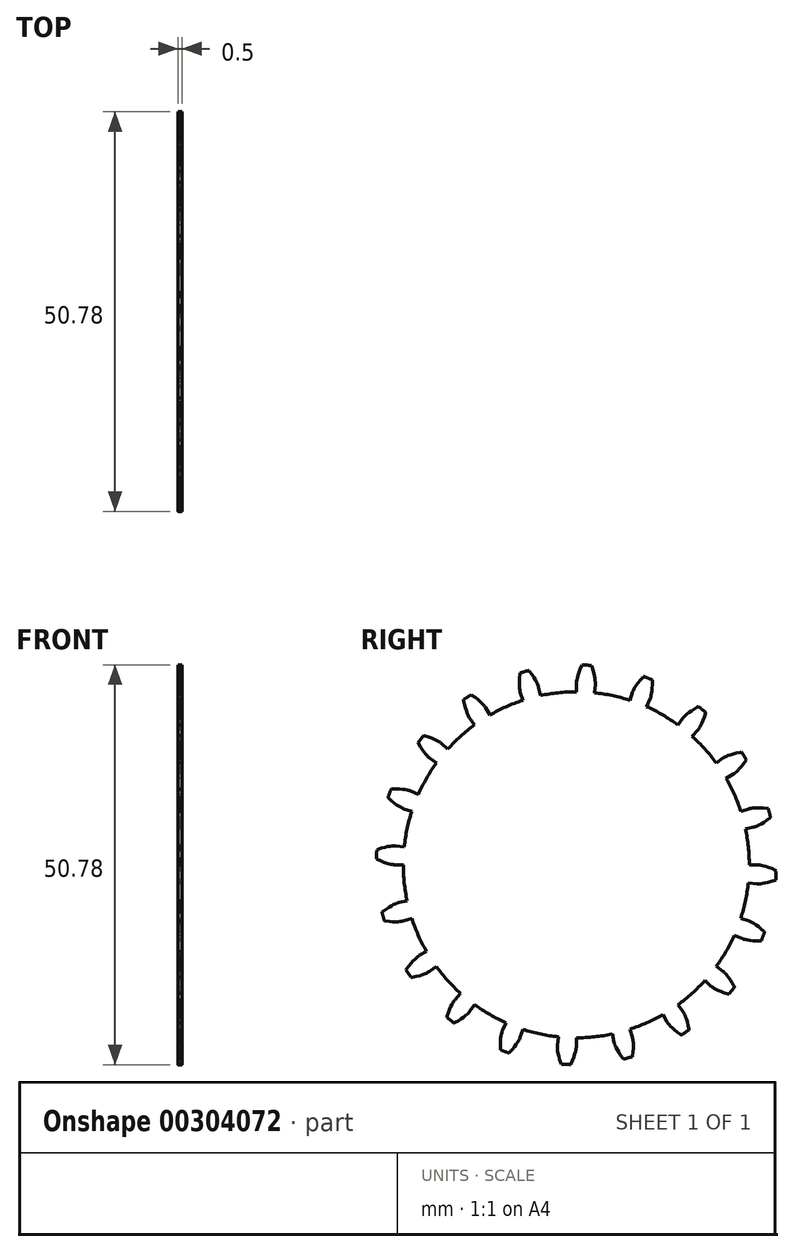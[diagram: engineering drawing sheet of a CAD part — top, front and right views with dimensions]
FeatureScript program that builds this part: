
annotation { "Feature Type Name" : "Feature", "Feature Type Description" : "" }
export const myFeature = defineFeature(function(context is Context, id is Id, definition is map)
    precondition{}
    {
        {
            assignVariable(context, id + "F0", {"name" : "GearThickness", "anyValue" : .5});
        }
        {
            var Q0;
            Q0=qCreatedBy(makeId("Right.planeOp"),FACE);
            var sketch = newSketch(context, id + "F1", { "sketchPlane" : qUnion([Q0])});
            skCircle(sketch, "E0", {"center": v(0, 0) * mm, "radius": 21.98 * mm});
            skCircle(sketch, "E1", {"center": v(0, 0) * mm, "radius": 23.05 * mm, "construction": true});
            skCircle(sketch, "E2", {"center": v(0, 0) * mm, "radius": 23.81 * mm, "construction": true});
            skCircle(sketch, "E3", {"center": v(0, 0) * mm, "radius": 25.4 * mm});
            skLineSegment(sketch, "E4", {"start": v(0, 0) * mm, "end": v(-23.05, 0) * mm, "construction": true});
            skLineSegment(sketch, "E5.1.0", {"start": v(0, 0) * mm, "end": v(-23.03, 1.15) * mm, "construction": true});
            skLineSegment(sketch, "E5.2.0", {"start": v(0, 0) * mm, "end": v(-22.94, 2.3) * mm, "construction": true});
            skLineSegment(sketch, "E5.3.0", {"start": v(0, 0) * mm, "end": v(-22.8, 3.45) * mm, "construction": true});
            skLineSegment(sketch, "E5.4.0", {"start": v(0, 0) * mm, "end": v(-22.6, 4.58) * mm, "construction": true});
            skLineSegment(sketch, "E5.5.0", {"start": v(0, 0) * mm, "end": v(-22.34, 5.7) * mm, "construction": true});
            skLineSegment(sketch, "E5.6.0", {"start": v(0, 0) * mm, "end": v(-22.02, 6.81) * mm, "construction": true});
            skLineSegment(sketch, "E5.7.0", {"start": v(0, 0) * mm, "end": v(-21.66, 7.9) * mm, "construction": true});
            skLineSegment(sketch, "E5.8.0", {"start": v(0, 0) * mm, "end": v(-21.23, 8.98) * mm, "construction": true});
            skLineSegment(sketch, "E5.9.0", {"start": v(0, 0) * mm, "end": v(-20.76, 10.03) * mm, "construction": true});
            skLineSegment(sketch, "E5.10.0", {"start": v(0, 0) * mm, "end": v(-20.23, 11.05) * mm, "construction": true});
            skLineSegment(sketch, "E5.11.0", {"start": v(0, 0) * mm, "end": v(-19.65, 12.05) * mm, "construction": true});
            skLineSegment(sketch, "E5.12.0", {"start": v(0, 0) * mm, "end": v(-19.03, 13.02) * mm, "construction": true});
            skLineSegment(sketch, "E5.13.0", {"start": v(0, 0) * mm, "end": v(-18.35, 13.95) * mm, "construction": true});
            skLineSegment(sketch, "E5.14.0", {"start": v(0, 0) * mm, "end": v(-17.63, 14.85) * mm, "construction": true});
            skLineSegment(sketch, "E5.anchor2", {"start": v(0, 0) * mm, "end": v(-17.63, 14.85) * mm, "construction": true});
            skLineSegment(sketch, "E6", {"start": v(-23.03, 1.15) * mm, "end": v(-23.08, 0) * mm, "construction": true});
            skLineSegment(sketch, "E7", {"start": v(-22.94, 2.3) * mm, "end": v(-23.17, 0) * mm, "construction": true});
            skLineSegment(sketch, "E8", {"start": v(-22.8, 3.45) * mm, "end": v(-23.31, 0.03) * mm, "construction": true});
            skLineSegment(sketch, "E9", {"start": v(-22.34, 5.7) * mm, "end": v(-23.76, 0.12) * mm, "construction": true});
            skLineSegment(sketch, "E10", {"start": v(-22.02, 6.81) * mm, "end": v(-24.07, 0.2) * mm, "construction": true});
            skLineSegment(sketch, "E11", {"start": v(-21.66, 7.9) * mm, "end": v(-24.42, 0.33) * mm, "construction": true});
            skLineSegment(sketch, "E12", {"start": v(-21.23, 8.98) * mm, "end": v(-24.83, 0.48) * mm, "construction": true});
            skLineSegment(sketch, "E13", {"start": v(-20.76, 10.03) * mm, "end": v(-25.27, 0.69) * mm, "construction": true});
            skLineSegment(sketch, "E14", {"start": v(-20.23, 11.05) * mm, "end": v(-25.76, 0.94) * mm, "construction": true});
            skLineSegment(sketch, "E15", {"start": v(-19.65, 12.05) * mm, "end": v(-26.28, 1.24) * mm, "construction": true});
            skLineSegment(sketch, "E16", {"start": v(-22.6, 4.58) * mm, "end": v(-23.51, 0.06) * mm, "construction": true});
            skLineSegment(sketch, "E17", {"start": v(-19.03, 13.02) * mm, "end": v(-26.84, 1.6) * mm, "construction": true});
            skLineSegment(sketch, "E18", {"start": v(-18.35, 13.95) * mm, "end": v(-27.42, 2.02) * mm, "construction": true});
            skLineSegment(sketch, "E19", {"start": v(-17.63, 14.85) * mm, "end": v(-28.03, 2.5) * mm, "construction": true});
            skLineSegment(sketch, "E20", {"start": v(0, 0) * mm, "end": v(-23.02, 1.2) * mm, "construction": true});
            skLineSegment(sketch, "E21", {"start": v(-21.98, 0) * mm, "end": v(-23.05, 0) * mm});
            skLineSegment(sketch, "E22.MirrorCS", {"start": v(-21.86, 2.3) * mm, "end": v(-22.93, 2.4) * mm});
            skLineSegment(sketch, "E23", {"start": v(-23.05, 0) * mm, "end": v(-23.08, 0) * mm});
            skLineSegment(sketch, "E24", {"start": v(-23.08, 0) * mm, "end": v(-23.17, 0) * mm});
            skLineSegment(sketch, "E25", {"start": v(-23.17, 0) * mm, "end": v(-23.31, 0.03) * mm});
            skLineSegment(sketch, "E26", {"start": v(-23.31, 0.03) * mm, "end": v(-23.51, 0.06) * mm});
            skLineSegment(sketch, "E27", {"start": v(-23.51, 0.06) * mm, "end": v(-23.76, 0.12) * mm});
            skLineSegment(sketch, "E28", {"start": v(-23.76, 0.12) * mm, "end": v(-24.07, 0.2) * mm});
            skLineSegment(sketch, "E29", {"start": v(-24.07, 0.2) * mm, "end": v(-24.42, 0.33) * mm});
            skLineSegment(sketch, "E30", {"start": v(-24.42, 0.33) * mm, "end": v(-24.83, 0.48) * mm});
            skLineSegment(sketch, "E31", {"start": v(-24.83, 0.48) * mm, "end": v(-25.27, 0.69) * mm});
            skLineSegment(sketch, "E32", {"start": v(-25.27, 0.69) * mm, "end": v(-25.76, 0.94) * mm});
            skLineSegment(sketch, "E33", {"start": v(-25.76, 0.94) * mm, "end": v(-26.28, 1.24) * mm});
            skLineSegment(sketch, "E34", {"start": v(-26.28, 1.24) * mm, "end": v(-26.84, 1.6) * mm});
            skLineSegment(sketch, "E35", {"start": v(-26.84, 1.6) * mm, "end": v(-27.42, 2.02) * mm});
            skLineSegment(sketch, "E36", {"start": v(-27.42, 2.02) * mm, "end": v(-28.03, 2.5) * mm});
            skLineSegment(sketch, "E37.MirrorCS", {"start": v(-22.93, 2.4) * mm, "end": v(-22.96, 2.41) * mm});
            skLineSegment(sketch, "E38.MirrorCS", {"start": v(-22.96, 2.41) * mm, "end": v(-23.04, 2.41) * mm});
            skLineSegment(sketch, "E39.MirrorCS", {"start": v(-23.04, 2.41) * mm, "end": v(-23.19, 2.41) * mm});
            skLineSegment(sketch, "E40.MirrorCS", {"start": v(-23.19, 2.41) * mm, "end": v(-23.39, 2.4) * mm});
            skLineSegment(sketch, "E41.MirrorCS", {"start": v(-23.65, 2.37) * mm, "end": v(-23.96, 2.31) * mm});
            skLineSegment(sketch, "E42.MirrorCS", {"start": v(-23.96, 2.31) * mm, "end": v(-24.32, 2.23) * mm});
            skLineSegment(sketch, "E43.MirrorCS", {"start": v(-24.32, 2.23) * mm, "end": v(-24.74, 2.11) * mm});
            skLineSegment(sketch, "E44.MirrorCS", {"start": v(-24.74, 2.11) * mm, "end": v(-25.2, 1.96) * mm});
            skLineSegment(sketch, "E45.MirrorCS", {"start": v(-25.71, 1.76) * mm, "end": v(-26.27, 1.51) * mm});
            skLineSegment(sketch, "E46.MirrorCS", {"start": v(-25.2, 1.96) * mm, "end": v(-25.71, 1.76) * mm});
            skLineSegment(sketch, "E47.MirrorCS", {"start": v(-26.27, 1.51) * mm, "end": v(-26.86, 1.21) * mm});
            skLineSegment(sketch, "E48.MirrorCS", {"start": v(-26.86, 1.21) * mm, "end": v(-27.48, 0.85) * mm});
            skLineSegment(sketch, "E49.MirrorCS", {"start": v(-27.48, 0.85) * mm, "end": v(-28.14, 0.43) * mm});
            skLineSegment(sketch, "E50.MirrorCS", {"start": v(-23.39, 2.4) * mm, "end": v(-23.65, 2.37) * mm});
            skLineSegment(sketch, "E51.1.0", {"start": v(-20.9, -6.8) * mm, "end": v(-21.93, -7.12) * mm});
            skLineSegment(sketch, "E51.1.1", {"start": v(-25.45, -6.68) * mm, "end": v(-25.92, -7.15) * mm});
            skLineSegment(sketch, "E51.1.2", {"start": v(-21.5, -4.57) * mm, "end": v(-22.55, -4.8) * mm});
            skLineSegment(sketch, "E51.1.3", {"start": v(-25, -6.27) * mm, "end": v(-25.45, -6.68) * mm});
            skLineSegment(sketch, "E51.1.4", {"start": v(-24.79, -7.07) * mm, "end": v(-25.38, -6.94) * mm});
            skLineSegment(sketch, "E51.1.5", {"start": v(-25.38, -6.94) * mm, "end": v(-26.02, -6.77) * mm});
            skLineSegment(sketch, "E51.1.6", {"start": v(-24.58, -5.93) * mm, "end": v(-25, -6.27) * mm});
            skLineSegment(sketch, "E51.1.7", {"start": v(-26.4, -7.68) * mm, "end": v(-26.9, -8.28) * mm});
            skLineSegment(sketch, "E51.1.8", {"start": v(-24.18, -5.63) * mm, "end": v(-24.58, -5.93) * mm});
            skLineSegment(sketch, "E51.1.9", {"start": v(-26.7, -6.55) * mm, "end": v(-27.43, -6.28) * mm});
            skLineSegment(sketch, "E51.1.10", {"start": v(-25.92, -7.15) * mm, "end": v(-26.4, -7.68) * mm});
            skLineSegment(sketch, "E51.1.11", {"start": v(-24.25, -7.16) * mm, "end": v(-24.79, -7.07) * mm});
            skLineSegment(sketch, "E51.1.12", {"start": v(-26.02, -6.77) * mm, "end": v(-26.7, -6.55) * mm});
            skLineSegment(sketch, "E51.1.13", {"start": v(-23.22, -5.06) * mm, "end": v(-23.5, -5.2) * mm});
            skLineSegment(sketch, "E51.1.14", {"start": v(-23.5, -5.2) * mm, "end": v(-23.82, -5.4) * mm});
            skLineSegment(sketch, "E51.1.15", {"start": v(-23.82, -5.4) * mm, "end": v(-24.18, -5.63) * mm});
            skLineSegment(sketch, "E51.1.16", {"start": v(-23.33, -7.24) * mm, "end": v(-23.76, -7.21) * mm});
            skLineSegment(sketch, "E51.1.17", {"start": v(-22.95, -7.24) * mm, "end": v(-23.33, -7.24) * mm});
            skLineSegment(sketch, "E51.1.18", {"start": v(-23.76, -7.21) * mm, "end": v(-24.25, -7.16) * mm});
            skLineSegment(sketch, "E51.1.19", {"start": v(-22.98, -4.95) * mm, "end": v(-23.22, -5.06) * mm});
            skLineSegment(sketch, "E51.1.20", {"start": v(-22.8, -4.87) * mm, "end": v(-22.98, -4.95) * mm});
            skLineSegment(sketch, "E51.1.21", {"start": v(-22.64, -7.23) * mm, "end": v(-22.95, -7.24) * mm});
            skLineSegment(sketch, "E51.1.22", {"start": v(-22.38, -7.2) * mm, "end": v(-22.64, -7.23) * mm});
            skLineSegment(sketch, "E51.1.23", {"start": v(-22.04, -7.15) * mm, "end": v(-22.18, -7.18) * mm});
            skLineSegment(sketch, "E51.1.24", {"start": v(-22.55, -4.8) * mm, "end": v(-22.58, -4.8) * mm});
            skLineSegment(sketch, "E51.1.25", {"start": v(-22.58, -4.8) * mm, "end": v(-22.66, -4.82) * mm});
            skLineSegment(sketch, "E51.1.26", {"start": v(-22.18, -7.18) * mm, "end": v(-22.38, -7.2) * mm});
            skLineSegment(sketch, "E51.1.27", {"start": v(-22.66, -4.82) * mm, "end": v(-22.8, -4.87) * mm});
            skLineSegment(sketch, "E51.1.28", {"start": v(-21.95, -7.13) * mm, "end": v(-22.04, -7.15) * mm});
            skLineSegment(sketch, "E51.1.29", {"start": v(-21.93, -7.12) * mm, "end": v(-21.95, -7.13) * mm});
            skLineSegment(sketch, "E51.2.0", {"start": v(-17.78, -12.92) * mm, "end": v(-18.65, -13.55) * mm});
            skLineSegment(sketch, "E51.2.1", {"start": v(-22.14, -14.21) * mm, "end": v(-22.44, -14.8) * mm});
            skLineSegment(sketch, "E51.2.2", {"start": v(-19.03, -10.99) * mm, "end": v(-19.97, -11.53) * mm});
            skLineSegment(sketch, "E51.2.3", {"start": v(-21.84, -13.7) * mm, "end": v(-22.14, -14.21) * mm});
            skLineSegment(sketch, "E51.2.4", {"start": v(-21.39, -14.38) * mm, "end": v(-22, -14.44) * mm});
            skLineSegment(sketch, "E51.2.5", {"start": v(-22, -14.44) * mm, "end": v(-22.65, -14.48) * mm});
            skLineSegment(sketch, "E51.2.6", {"start": v(-21.54, -13.23) * mm, "end": v(-21.84, -13.7) * mm});
            skLineSegment(sketch, "E51.2.7", {"start": v(-22.74, -15.46) * mm, "end": v(-23.02, -16.19) * mm});
            skLineSegment(sketch, "E51.2.8", {"start": v(-21.26, -12.83) * mm, "end": v(-21.54, -13.23) * mm});
            skLineSegment(sketch, "E51.2.9", {"start": v(-23.37, -14.48) * mm, "end": v(-24.15, -14.45) * mm});
            skLineSegment(sketch, "E51.2.10", {"start": v(-22.44, -14.8) * mm, "end": v(-22.74, -15.46) * mm});
            skLineSegment(sketch, "E51.2.11", {"start": v(-20.85, -14.3) * mm, "end": v(-21.39, -14.38) * mm});
            skLineSegment(sketch, "E51.2.12", {"start": v(-22.65, -14.48) * mm, "end": v(-23.37, -14.48) * mm});
            skLineSegment(sketch, "E51.2.13", {"start": v(-20.52, -11.98) * mm, "end": v(-20.74, -12.21) * mm});
            skLineSegment(sketch, "E51.2.14", {"start": v(-20.74, -12.21) * mm, "end": v(-20.99, -12.5) * mm});
            skLineSegment(sketch, "E51.2.15", {"start": v(-20.99, -12.5) * mm, "end": v(-21.26, -12.83) * mm});
            skLineSegment(sketch, "E51.2.16", {"start": v(-19.95, -14.1) * mm, "end": v(-20.37, -14.2) * mm});
            skLineSegment(sketch, "E51.2.17", {"start": v(-19.6, -13.98) * mm, "end": v(-19.95, -14.1) * mm});
            skLineSegment(sketch, "E51.2.18", {"start": v(-20.37, -14.2) * mm, "end": v(-20.85, -14.3) * mm});
            skLineSegment(sketch, "E51.2.19", {"start": v(-20.33, -11.8) * mm, "end": v(-20.52, -11.98) * mm});
            skLineSegment(sketch, "E51.2.20", {"start": v(-20.18, -11.68) * mm, "end": v(-20.33, -11.8) * mm});
            skLineSegment(sketch, "E51.2.21", {"start": v(-19.3, -13.87) * mm, "end": v(-19.6, -13.98) * mm});
            skLineSegment(sketch, "E51.2.22", {"start": v(-19.06, -13.77) * mm, "end": v(-19.3, -13.87) * mm});
            skLineSegment(sketch, "E51.2.23", {"start": v(-18.75, -13.61) * mm, "end": v(-18.87, -13.68) * mm});
            skLineSegment(sketch, "E51.2.24", {"start": v(-19.97, -11.53) * mm, "end": v(-19.99, -11.54) * mm});
            skLineSegment(sketch, "E51.2.25", {"start": v(-19.99, -11.54) * mm, "end": v(-20.06, -11.6) * mm});
            skLineSegment(sketch, "E51.2.26", {"start": v(-18.87, -13.68) * mm, "end": v(-19.06, -13.77) * mm});
            skLineSegment(sketch, "E51.2.27", {"start": v(-20.06, -11.6) * mm, "end": v(-20.18, -11.68) * mm});
            skLineSegment(sketch, "E51.2.28", {"start": v(-18.67, -13.57) * mm, "end": v(-18.75, -13.61) * mm});
            skLineSegment(sketch, "E51.2.29", {"start": v(-18.65, -13.55) * mm, "end": v(-18.67, -13.57) * mm});
            skLineSegment(sketch, "E51.3.0", {"start": v(-12.92, -17.78) * mm, "end": v(-13.55, -18.65) * mm});
            skLineSegment(sketch, "E51.3.1", {"start": v(-16.66, -20.36) * mm, "end": v(-16.77, -21.02) * mm});
            skLineSegment(sketch, "E51.3.2", {"start": v(-14.7, -16.33) * mm, "end": v(-15.43, -17.13) * mm});
            skLineSegment(sketch, "E51.3.3", {"start": v(-16.54, -19.77) * mm, "end": v(-16.66, -20.36) * mm});
            skLineSegment(sketch, "E51.3.4", {"start": v(-15.9, -20.29) * mm, "end": v(-16.45, -20.53) * mm});
            skLineSegment(sketch, "E51.3.5", {"start": v(-16.45, -20.53) * mm, "end": v(-17.07, -20.77) * mm});
            skLineSegment(sketch, "E51.3.6", {"start": v(-16.4, -19.24) * mm, "end": v(-16.54, -19.77) * mm});
            skLineSegment(sketch, "E51.3.7", {"start": v(-16.85, -21.73) * mm, "end": v(-16.9, -22.5) * mm});
            skLineSegment(sketch, "E51.3.8", {"start": v(-16.25, -18.77) * mm, "end": v(-16.4, -19.24) * mm});
            skLineSegment(sketch, "E51.3.9", {"start": v(-17.75, -21) * mm, "end": v(-18.5, -21.2) * mm});
            skLineSegment(sketch, "E51.3.10", {"start": v(-16.77, -21.02) * mm, "end": v(-16.85, -21.73) * mm});
            skLineSegment(sketch, "E51.3.11", {"start": v(-15.4, -20.04) * mm, "end": v(-15.9, -20.29) * mm});
            skLineSegment(sketch, "E51.3.12", {"start": v(-17.07, -20.77) * mm, "end": v(-17.75, -21) * mm});
            skLineSegment(sketch, "E51.3.13", {"start": v(-15.81, -17.74) * mm, "end": v(-15.95, -18.02) * mm});
            skLineSegment(sketch, "E51.3.14", {"start": v(-15.95, -18.02) * mm, "end": v(-16.1, -18.37) * mm});
            skLineSegment(sketch, "E51.3.15", {"start": v(-16.1, -18.37) * mm, "end": v(-16.25, -18.77) * mm});
            skLineSegment(sketch, "E51.3.16", {"start": v(-14.62, -19.57) * mm, "end": v(-14.98, -19.8) * mm});
            skLineSegment(sketch, "E51.3.17", {"start": v(-14.31, -19.35) * mm, "end": v(-14.62, -19.57) * mm});
            skLineSegment(sketch, "E51.3.18", {"start": v(-14.98, -19.8) * mm, "end": v(-15.4, -20.04) * mm});
            skLineSegment(sketch, "E51.3.19", {"start": v(-15.69, -17.51) * mm, "end": v(-15.81, -17.74) * mm});
            skLineSegment(sketch, "E51.3.20", {"start": v(-15.58, -17.34) * mm, "end": v(-15.69, -17.51) * mm});
            skLineSegment(sketch, "E51.3.21", {"start": v(-14.06, -19.15) * mm, "end": v(-14.31, -19.35) * mm});
            skLineSegment(sketch, "E51.3.22", {"start": v(-13.87, -18.98) * mm, "end": v(-14.06, -19.15) * mm});
            skLineSegment(sketch, "E51.3.23", {"start": v(-13.62, -18.74) * mm, "end": v(-13.72, -18.84) * mm});
            skLineSegment(sketch, "E51.3.24", {"start": v(-15.43, -17.13) * mm, "end": v(-15.44, -17.15) * mm});
            skLineSegment(sketch, "E51.3.25", {"start": v(-15.44, -17.15) * mm, "end": v(-15.5, -17.22) * mm});
            skLineSegment(sketch, "E51.3.26", {"start": v(-13.72, -18.84) * mm, "end": v(-13.87, -18.98) * mm});
            skLineSegment(sketch, "E51.3.27", {"start": v(-15.5, -17.22) * mm, "end": v(-15.58, -17.34) * mm});
            skLineSegment(sketch, "E51.3.28", {"start": v(-13.57, -18.67) * mm, "end": v(-13.62, -18.74) * mm});
            skLineSegment(sketch, "E51.3.29", {"start": v(-13.55, -18.65) * mm, "end": v(-13.57, -18.67) * mm});
            skLineSegment(sketch, "E51.4.0", {"start": v(-6.8, -20.9) * mm, "end": v(-7.12, -21.93) * mm});
            skLineSegment(sketch, "E51.4.1", {"start": v(-9.56, -24.51) * mm, "end": v(-9.45, -25.17) * mm});
            skLineSegment(sketch, "E51.4.2", {"start": v(-8.94, -20.08) * mm, "end": v(-9.38, -21.06) * mm});
            skLineSegment(sketch, "E51.4.3", {"start": v(-9.62, -23.91) * mm, "end": v(-9.56, -24.51) * mm});
            skLineSegment(sketch, "E51.4.4", {"start": v(-8.85, -24.2) * mm, "end": v(-9.3, -24.61) * mm});
            skLineSegment(sketch, "E51.4.5", {"start": v(-9.3, -24.61) * mm, "end": v(-9.82, -25.03) * mm});
            skLineSegment(sketch, "E51.4.6", {"start": v(-9.65, -23.37) * mm, "end": v(-9.62, -23.91) * mm});
            skLineSegment(sketch, "E51.4.7", {"start": v(-9.3, -25.87) * mm, "end": v(-9.1, -26.63) * mm});
            skLineSegment(sketch, "E51.4.8", {"start": v(-9.66, -22.88) * mm, "end": v(-9.65, -23.37) * mm});
            skLineSegment(sketch, "E51.4.9", {"start": v(-10.4, -25.45) * mm, "end": v(-11.05, -25.88) * mm});
            skLineSegment(sketch, "E51.4.10", {"start": v(-9.45, -25.17) * mm, "end": v(-9.3, -25.87) * mm});
            skLineSegment(sketch, "E51.4.11", {"start": v(-8.46, -23.82) * mm, "end": v(-8.85, -24.2) * mm});
            skLineSegment(sketch, "E51.4.12", {"start": v(-9.82, -25.03) * mm, "end": v(-10.4, -25.45) * mm});
            skLineSegment(sketch, "E51.4.13", {"start": v(-9.56, -21.76) * mm, "end": v(-9.6, -22.07) * mm});
            skLineSegment(sketch, "E51.4.14", {"start": v(-9.6, -22.07) * mm, "end": v(-9.64, -22.44) * mm});
            skLineSegment(sketch, "E51.4.15", {"start": v(-9.64, -22.44) * mm, "end": v(-9.66, -22.88) * mm});
            skLineSegment(sketch, "E51.4.16", {"start": v(-7.86, -23.13) * mm, "end": v(-8.13, -23.46) * mm});
            skLineSegment(sketch, "E51.4.17", {"start": v(-7.63, -22.83) * mm, "end": v(-7.86, -23.13) * mm});
            skLineSegment(sketch, "E51.4.18", {"start": v(-8.13, -23.46) * mm, "end": v(-8.46, -23.82) * mm});
            skLineSegment(sketch, "E51.4.19", {"start": v(-9.5, -21.5) * mm, "end": v(-9.56, -21.76) * mm});
            skLineSegment(sketch, "E51.4.20", {"start": v(-9.46, -21.3) * mm, "end": v(-9.5, -21.5) * mm});
            skLineSegment(sketch, "E51.4.21", {"start": v(-7.46, -22.56) * mm, "end": v(-7.63, -22.83) * mm});
            skLineSegment(sketch, "E51.4.22", {"start": v(-7.32, -22.34) * mm, "end": v(-7.46, -22.56) * mm});
            skLineSegment(sketch, "E51.4.23", {"start": v(-7.17, -22.03) * mm, "end": v(-7.23, -22.16) * mm});
            skLineSegment(sketch, "E51.4.24", {"start": v(-9.38, -21.06) * mm, "end": v(-9.39, -21.09) * mm});
            skLineSegment(sketch, "E51.4.25", {"start": v(-9.39, -21.09) * mm, "end": v(-9.42, -21.17) * mm});
            skLineSegment(sketch, "E51.4.26", {"start": v(-7.23, -22.16) * mm, "end": v(-7.32, -22.34) * mm});
            skLineSegment(sketch, "E51.4.27", {"start": v(-9.42, -21.17) * mm, "end": v(-9.46, -21.3) * mm});
            skLineSegment(sketch, "E51.4.28", {"start": v(-7.13, -21.95) * mm, "end": v(-7.17, -22.03) * mm});
            skLineSegment(sketch, "E51.4.29", {"start": v(-7.12, -21.93) * mm, "end": v(-7.13, -21.95) * mm});
            skLineSegment(sketch, "E51.5.0", {"start": v(0, -21.98) * mm, "end": v(0, -23.05) * mm});
            skLineSegment(sketch, "E51.5.1", {"start": v(-1.51, -26.27) * mm, "end": v(-1.21, -26.86) * mm});
            skLineSegment(sketch, "E51.5.2", {"start": v(-2.3, -21.86) * mm, "end": v(-2.4, -22.93) * mm});
            skLineSegment(sketch, "E51.5.3", {"start": v(-1.76, -25.71) * mm, "end": v(-1.51, -26.27) * mm});
            skLineSegment(sketch, "E51.5.4", {"start": v(-0.94, -25.76) * mm, "end": v(-1.24, -26.28) * mm});
            skLineSegment(sketch, "E51.5.5", {"start": v(-1.24, -26.28) * mm, "end": v(-1.6, -26.84) * mm});
            skLineSegment(sketch, "E51.5.6", {"start": v(-1.96, -25.2) * mm, "end": v(-1.76, -25.71) * mm});
            skLineSegment(sketch, "E51.5.7", {"start": v(-0.85, -27.48) * mm, "end": v(-0.43, -28.14) * mm});
            skLineSegment(sketch, "E51.5.8", {"start": v(-2.11, -24.74) * mm, "end": v(-1.96, -25.2) * mm});
            skLineSegment(sketch, "E51.5.9", {"start": v(-2.02, -27.42) * mm, "end": v(-2.5, -28.03) * mm});
            skLineSegment(sketch, "E51.5.10", {"start": v(-1.21, -26.86) * mm, "end": v(-0.85, -27.48) * mm});
            skLineSegment(sketch, "E51.5.11", {"start": v(-0.69, -25.27) * mm, "end": v(-0.94, -25.76) * mm});
            skLineSegment(sketch, "E51.5.12", {"start": v(-1.6, -26.84) * mm, "end": v(-2.02, -27.42) * mm});
            skLineSegment(sketch, "E51.5.13", {"start": v(-2.37, -23.65) * mm, "end": v(-2.31, -23.96) * mm});
            skLineSegment(sketch, "E51.5.14", {"start": v(-2.31, -23.96) * mm, "end": v(-2.23, -24.32) * mm});
            skLineSegment(sketch, "E51.5.15", {"start": v(-2.23, -24.32) * mm, "end": v(-2.11, -24.74) * mm});
            skLineSegment(sketch, "E51.5.16", {"start": v(-0.33, -24.42) * mm, "end": v(-0.48, -24.83) * mm});
            skLineSegment(sketch, "E51.5.17", {"start": v(-0.2, -24.07) * mm, "end": v(-0.33, -24.42) * mm});
            skLineSegment(sketch, "E51.5.18", {"start": v(-0.48, -24.83) * mm, "end": v(-0.69, -25.27) * mm});
            skLineSegment(sketch, "E51.5.19", {"start": v(-2.4, -23.39) * mm, "end": v(-2.37, -23.65) * mm});
            skLineSegment(sketch, "E51.5.20", {"start": v(-2.41, -23.19) * mm, "end": v(-2.4, -23.39) * mm});
            skLineSegment(sketch, "E51.5.21", {"start": v(-0.12, -23.76) * mm, "end": v(-0.2, -24.07) * mm});
            skLineSegment(sketch, "E51.5.22", {"start": v(-0.06, -23.51) * mm, "end": v(-0.12, -23.76) * mm});
            skLineSegment(sketch, "E51.5.23", {"start": v(0, -23.17) * mm, "end": v(-0.03, -23.31) * mm});
            skLineSegment(sketch, "E51.5.24", {"start": v(-2.4, -22.93) * mm, "end": v(-2.41, -22.96) * mm});
            skLineSegment(sketch, "E51.5.25", {"start": v(-2.41, -22.96) * mm, "end": v(-2.41, -23.04) * mm});
            skLineSegment(sketch, "E51.5.26", {"start": v(-0.03, -23.31) * mm, "end": v(-0.06, -23.51) * mm});
            skLineSegment(sketch, "E51.5.27", {"start": v(-2.41, -23.04) * mm, "end": v(-2.41, -23.19) * mm});
            skLineSegment(sketch, "E51.5.28", {"start": v(0, -23.08) * mm, "end": v(0, -23.17) * mm});
            skLineSegment(sketch, "E51.5.29", {"start": v(0, -23.05) * mm, "end": v(0, -23.08) * mm});
            skLineSegment(sketch, "E51.6.0", {"start": v(6.8, -20.9) * mm, "end": v(7.12, -21.93) * mm});
            skLineSegment(sketch, "E51.6.1", {"start": v(6.68, -25.45) * mm, "end": v(7.15, -25.92) * mm});
            skLineSegment(sketch, "E51.6.2", {"start": v(4.57, -21.5) * mm, "end": v(4.8, -22.55) * mm});
            skLineSegment(sketch, "E51.6.3", {"start": v(6.27, -25) * mm, "end": v(6.68, -25.45) * mm});
            skLineSegment(sketch, "E51.6.4", {"start": v(7.07, -24.79) * mm, "end": v(6.94, -25.38) * mm});
            skLineSegment(sketch, "E51.6.5", {"start": v(6.94, -25.38) * mm, "end": v(6.77, -26.02) * mm});
            skLineSegment(sketch, "E51.6.6", {"start": v(5.93, -24.58) * mm, "end": v(6.27, -25) * mm});
            skLineSegment(sketch, "E51.6.7", {"start": v(7.68, -26.4) * mm, "end": v(8.28, -26.9) * mm});
            skLineSegment(sketch, "E51.6.8", {"start": v(5.63, -24.18) * mm, "end": v(5.93, -24.58) * mm});
            skLineSegment(sketch, "E51.6.9", {"start": v(6.55, -26.7) * mm, "end": v(6.28, -27.43) * mm});
            skLineSegment(sketch, "E51.6.10", {"start": v(7.15, -25.92) * mm, "end": v(7.68, -26.4) * mm});
            skLineSegment(sketch, "E51.6.11", {"start": v(7.16, -24.25) * mm, "end": v(7.07, -24.79) * mm});
            skLineSegment(sketch, "E51.6.12", {"start": v(6.77, -26.02) * mm, "end": v(6.55, -26.7) * mm});
            skLineSegment(sketch, "E51.6.13", {"start": v(5.06, -23.22) * mm, "end": v(5.2, -23.5) * mm});
            skLineSegment(sketch, "E51.6.14", {"start": v(5.2, -23.5) * mm, "end": v(5.4, -23.82) * mm});
            skLineSegment(sketch, "E51.6.15", {"start": v(5.4, -23.82) * mm, "end": v(5.63, -24.18) * mm});
            skLineSegment(sketch, "E51.6.16", {"start": v(7.24, -23.33) * mm, "end": v(7.21, -23.76) * mm});
            skLineSegment(sketch, "E51.6.17", {"start": v(7.24, -22.95) * mm, "end": v(7.24, -23.33) * mm});
            skLineSegment(sketch, "E51.6.18", {"start": v(7.21, -23.76) * mm, "end": v(7.16, -24.25) * mm});
            skLineSegment(sketch, "E51.6.19", {"start": v(4.95, -22.98) * mm, "end": v(5.06, -23.22) * mm});
            skLineSegment(sketch, "E51.6.20", {"start": v(4.87, -22.8) * mm, "end": v(4.95, -22.98) * mm});
            skLineSegment(sketch, "E51.6.21", {"start": v(7.23, -22.64) * mm, "end": v(7.24, -22.95) * mm});
            skLineSegment(sketch, "E51.6.22", {"start": v(7.2, -22.38) * mm, "end": v(7.23, -22.64) * mm});
            skLineSegment(sketch, "E51.6.23", {"start": v(7.15, -22.04) * mm, "end": v(7.18, -22.18) * mm});
            skLineSegment(sketch, "E51.6.24", {"start": v(4.8, -22.55) * mm, "end": v(4.8, -22.58) * mm});
            skLineSegment(sketch, "E51.6.25", {"start": v(4.8, -22.58) * mm, "end": v(4.82, -22.66) * mm});
            skLineSegment(sketch, "E51.6.26", {"start": v(7.18, -22.18) * mm, "end": v(7.2, -22.38) * mm});
            skLineSegment(sketch, "E51.6.27", {"start": v(4.82, -22.66) * mm, "end": v(4.87, -22.8) * mm});
            skLineSegment(sketch, "E51.6.28", {"start": v(7.13, -21.95) * mm, "end": v(7.15, -22.04) * mm});
            skLineSegment(sketch, "E51.6.29", {"start": v(7.12, -21.93) * mm, "end": v(7.13, -21.95) * mm});
            skLineSegment(sketch, "E51.7.0", {"start": v(12.92, -17.78) * mm, "end": v(13.55, -18.65) * mm});
            skLineSegment(sketch, "E51.7.1", {"start": v(14.21, -22.14) * mm, "end": v(14.8, -22.44) * mm});
            skLineSegment(sketch, "E51.7.2", {"start": v(10.99, -19.03) * mm, "end": v(11.53, -19.97) * mm});
            skLineSegment(sketch, "E51.7.3", {"start": v(13.7, -21.84) * mm, "end": v(14.21, -22.14) * mm});
            skLineSegment(sketch, "E51.7.4", {"start": v(14.38, -21.39) * mm, "end": v(14.44, -22) * mm});
            skLineSegment(sketch, "E51.7.5", {"start": v(14.44, -22) * mm, "end": v(14.48, -22.65) * mm});
            skLineSegment(sketch, "E51.7.6", {"start": v(13.23, -21.54) * mm, "end": v(13.7, -21.84) * mm});
            skLineSegment(sketch, "E51.7.7", {"start": v(15.46, -22.74) * mm, "end": v(16.19, -23.02) * mm});
            skLineSegment(sketch, "E51.7.8", {"start": v(12.83, -21.26) * mm, "end": v(13.23, -21.54) * mm});
            skLineSegment(sketch, "E51.7.9", {"start": v(14.48, -23.37) * mm, "end": v(14.45, -24.15) * mm});
            skLineSegment(sketch, "E51.7.10", {"start": v(14.8, -22.44) * mm, "end": v(15.46, -22.74) * mm});
            skLineSegment(sketch, "E51.7.11", {"start": v(14.3, -20.85) * mm, "end": v(14.38, -21.39) * mm});
            skLineSegment(sketch, "E51.7.12", {"start": v(14.48, -22.65) * mm, "end": v(14.48, -23.37) * mm});
            skLineSegment(sketch, "E51.7.13", {"start": v(11.98, -20.52) * mm, "end": v(12.21, -20.74) * mm});
            skLineSegment(sketch, "E51.7.14", {"start": v(12.21, -20.74) * mm, "end": v(12.5, -20.99) * mm});
            skLineSegment(sketch, "E51.7.15", {"start": v(12.5, -20.99) * mm, "end": v(12.83, -21.26) * mm});
            skLineSegment(sketch, "E51.7.16", {"start": v(14.1, -19.95) * mm, "end": v(14.2, -20.37) * mm});
            skLineSegment(sketch, "E51.7.17", {"start": v(13.98, -19.6) * mm, "end": v(14.1, -19.95) * mm});
            skLineSegment(sketch, "E51.7.18", {"start": v(14.2, -20.37) * mm, "end": v(14.3, -20.85) * mm});
            skLineSegment(sketch, "E51.7.19", {"start": v(11.8, -20.33) * mm, "end": v(11.98, -20.52) * mm});
            skLineSegment(sketch, "E51.7.20", {"start": v(11.68, -20.18) * mm, "end": v(11.8, -20.33) * mm});
            skLineSegment(sketch, "E51.7.21", {"start": v(13.87, -19.3) * mm, "end": v(13.98, -19.6) * mm});
            skLineSegment(sketch, "E51.7.22", {"start": v(13.77, -19.06) * mm, "end": v(13.87, -19.3) * mm});
            skLineSegment(sketch, "E51.7.23", {"start": v(13.61, -18.75) * mm, "end": v(13.68, -18.87) * mm});
            skLineSegment(sketch, "E51.7.24", {"start": v(11.53, -19.97) * mm, "end": v(11.54, -19.99) * mm});
            skLineSegment(sketch, "E51.7.25", {"start": v(11.54, -19.99) * mm, "end": v(11.6, -20.06) * mm});
            skLineSegment(sketch, "E51.7.26", {"start": v(13.68, -18.87) * mm, "end": v(13.77, -19.06) * mm});
            skLineSegment(sketch, "E51.7.27", {"start": v(11.6, -20.06) * mm, "end": v(11.68, -20.18) * mm});
            skLineSegment(sketch, "E51.7.28", {"start": v(13.57, -18.67) * mm, "end": v(13.61, -18.75) * mm});
            skLineSegment(sketch, "E51.7.29", {"start": v(13.55, -18.65) * mm, "end": v(13.57, -18.67) * mm});
            skLineSegment(sketch, "E51.8.0", {"start": v(17.78, -12.92) * mm, "end": v(18.65, -13.55) * mm});
            skLineSegment(sketch, "E51.8.1", {"start": v(20.36, -16.66) * mm, "end": v(21.02, -16.77) * mm});
            skLineSegment(sketch, "E51.8.2", {"start": v(16.33, -14.7) * mm, "end": v(17.13, -15.43) * mm});
            skLineSegment(sketch, "E51.8.3", {"start": v(19.77, -16.54) * mm, "end": v(20.36, -16.66) * mm});
            skLineSegment(sketch, "E51.8.4", {"start": v(20.29, -15.9) * mm, "end": v(20.53, -16.45) * mm});
            skLineSegment(sketch, "E51.8.5", {"start": v(20.53, -16.45) * mm, "end": v(20.77, -17.07) * mm});
            skLineSegment(sketch, "E51.8.6", {"start": v(19.24, -16.4) * mm, "end": v(19.77, -16.54) * mm});
            skLineSegment(sketch, "E51.8.7", {"start": v(21.73, -16.85) * mm, "end": v(22.5, -16.9) * mm});
            skLineSegment(sketch, "E51.8.8", {"start": v(18.77, -16.25) * mm, "end": v(19.24, -16.4) * mm});
            skLineSegment(sketch, "E51.8.9", {"start": v(21, -17.75) * mm, "end": v(21.2, -18.5) * mm});
            skLineSegment(sketch, "E51.8.10", {"start": v(21.02, -16.77) * mm, "end": v(21.73, -16.85) * mm});
            skLineSegment(sketch, "E51.8.11", {"start": v(20.04, -15.4) * mm, "end": v(20.29, -15.9) * mm});
            skLineSegment(sketch, "E51.8.12", {"start": v(20.77, -17.07) * mm, "end": v(21, -17.75) * mm});
            skLineSegment(sketch, "E51.8.13", {"start": v(17.74, -15.81) * mm, "end": v(18.02, -15.95) * mm});
            skLineSegment(sketch, "E51.8.14", {"start": v(18.02, -15.95) * mm, "end": v(18.37, -16.1) * mm});
            skLineSegment(sketch, "E51.8.15", {"start": v(18.37, -16.1) * mm, "end": v(18.77, -16.25) * mm});
            skLineSegment(sketch, "E51.8.16", {"start": v(19.57, -14.62) * mm, "end": v(19.8, -14.98) * mm});
            skLineSegment(sketch, "E51.8.17", {"start": v(19.35, -14.31) * mm, "end": v(19.57, -14.62) * mm});
            skLineSegment(sketch, "E51.8.18", {"start": v(19.8, -14.98) * mm, "end": v(20.04, -15.4) * mm});
            skLineSegment(sketch, "E51.8.19", {"start": v(17.51, -15.69) * mm, "end": v(17.74, -15.81) * mm});
            skLineSegment(sketch, "E51.8.20", {"start": v(17.34, -15.58) * mm, "end": v(17.51, -15.69) * mm});
            skLineSegment(sketch, "E51.8.21", {"start": v(19.15, -14.06) * mm, "end": v(19.35, -14.31) * mm});
            skLineSegment(sketch, "E51.8.22", {"start": v(18.98, -13.87) * mm, "end": v(19.15, -14.06) * mm});
            skLineSegment(sketch, "E51.8.23", {"start": v(18.74, -13.62) * mm, "end": v(18.84, -13.72) * mm});
            skLineSegment(sketch, "E51.8.24", {"start": v(17.13, -15.43) * mm, "end": v(17.15, -15.44) * mm});
            skLineSegment(sketch, "E51.8.25", {"start": v(17.15, -15.44) * mm, "end": v(17.22, -15.5) * mm});
            skLineSegment(sketch, "E51.8.26", {"start": v(18.84, -13.72) * mm, "end": v(18.98, -13.87) * mm});
            skLineSegment(sketch, "E51.8.27", {"start": v(17.22, -15.5) * mm, "end": v(17.34, -15.58) * mm});
            skLineSegment(sketch, "E51.8.28", {"start": v(18.67, -13.57) * mm, "end": v(18.74, -13.62) * mm});
            skLineSegment(sketch, "E51.8.29", {"start": v(18.65, -13.55) * mm, "end": v(18.67, -13.57) * mm});
            skLineSegment(sketch, "E51.9.0", {"start": v(20.9, -6.8) * mm, "end": v(21.93, -7.12) * mm});
            skLineSegment(sketch, "E51.9.1", {"start": v(24.51, -9.56) * mm, "end": v(25.17, -9.45) * mm});
            skLineSegment(sketch, "E51.9.2", {"start": v(20.08, -8.94) * mm, "end": v(21.06, -9.38) * mm});
            skLineSegment(sketch, "E51.9.3", {"start": v(23.91, -9.62) * mm, "end": v(24.51, -9.56) * mm});
            skLineSegment(sketch, "E51.9.4", {"start": v(24.2, -8.85) * mm, "end": v(24.61, -9.3) * mm});
            skLineSegment(sketch, "E51.9.5", {"start": v(24.61, -9.3) * mm, "end": v(25.03, -9.82) * mm});
            skLineSegment(sketch, "E51.9.6", {"start": v(23.37, -9.65) * mm, "end": v(23.91, -9.62) * mm});
            skLineSegment(sketch, "E51.9.7", {"start": v(25.87, -9.3) * mm, "end": v(26.63, -9.1) * mm});
            skLineSegment(sketch, "E51.9.8", {"start": v(22.88, -9.66) * mm, "end": v(23.37, -9.65) * mm});
            skLineSegment(sketch, "E51.9.9", {"start": v(25.45, -10.4) * mm, "end": v(25.88, -11.05) * mm});
            skLineSegment(sketch, "E51.9.10", {"start": v(25.17, -9.45) * mm, "end": v(25.87, -9.3) * mm});
            skLineSegment(sketch, "E51.9.11", {"start": v(23.82, -8.46) * mm, "end": v(24.2, -8.85) * mm});
            skLineSegment(sketch, "E51.9.12", {"start": v(25.03, -9.82) * mm, "end": v(25.45, -10.4) * mm});
            skLineSegment(sketch, "E51.9.13", {"start": v(21.76, -9.56) * mm, "end": v(22.07, -9.6) * mm});
            skLineSegment(sketch, "E51.9.14", {"start": v(22.07, -9.6) * mm, "end": v(22.44, -9.64) * mm});
            skLineSegment(sketch, "E51.9.15", {"start": v(22.44, -9.64) * mm, "end": v(22.88, -9.66) * mm});
            skLineSegment(sketch, "E51.9.16", {"start": v(23.13, -7.86) * mm, "end": v(23.46, -8.13) * mm});
            skLineSegment(sketch, "E51.9.17", {"start": v(22.83, -7.63) * mm, "end": v(23.13, -7.86) * mm});
            skLineSegment(sketch, "E51.9.18", {"start": v(23.46, -8.13) * mm, "end": v(23.82, -8.46) * mm});
            skLineSegment(sketch, "E51.9.19", {"start": v(21.5, -9.5) * mm, "end": v(21.76, -9.56) * mm});
            skLineSegment(sketch, "E51.9.20", {"start": v(21.3, -9.46) * mm, "end": v(21.5, -9.5) * mm});
            skLineSegment(sketch, "E51.9.21", {"start": v(22.56, -7.46) * mm, "end": v(22.83, -7.63) * mm});
            skLineSegment(sketch, "E51.9.22", {"start": v(22.34, -7.32) * mm, "end": v(22.56, -7.46) * mm});
            skLineSegment(sketch, "E51.9.23", {"start": v(22.03, -7.17) * mm, "end": v(22.16, -7.23) * mm});
            skLineSegment(sketch, "E51.9.24", {"start": v(21.06, -9.38) * mm, "end": v(21.09, -9.39) * mm});
            skLineSegment(sketch, "E51.9.25", {"start": v(21.09, -9.39) * mm, "end": v(21.17, -9.42) * mm});
            skLineSegment(sketch, "E51.9.26", {"start": v(22.16, -7.23) * mm, "end": v(22.34, -7.32) * mm});
            skLineSegment(sketch, "E51.9.27", {"start": v(21.17, -9.42) * mm, "end": v(21.3, -9.46) * mm});
            skLineSegment(sketch, "E51.9.28", {"start": v(21.95, -7.13) * mm, "end": v(22.03, -7.17) * mm});
            skLineSegment(sketch, "E51.9.29", {"start": v(21.93, -7.12) * mm, "end": v(21.95, -7.13) * mm});
            skLineSegment(sketch, "E51.10.0", {"start": v(21.98, 0) * mm, "end": v(23.05, 0) * mm});
            skLineSegment(sketch, "E51.10.1", {"start": v(26.27, -1.51) * mm, "end": v(26.86, -1.21) * mm});
            skLineSegment(sketch, "E51.10.2", {"start": v(21.86, -2.3) * mm, "end": v(22.93, -2.4) * mm});
            skLineSegment(sketch, "E51.10.3", {"start": v(25.71, -1.76) * mm, "end": v(26.27, -1.51) * mm});
            skLineSegment(sketch, "E51.10.4", {"start": v(25.76, -0.94) * mm, "end": v(26.28, -1.24) * mm});
            skLineSegment(sketch, "E51.10.5", {"start": v(26.28, -1.24) * mm, "end": v(26.84, -1.6) * mm});
            skLineSegment(sketch, "E51.10.6", {"start": v(25.2, -1.96) * mm, "end": v(25.71, -1.76) * mm});
            skLineSegment(sketch, "E51.10.7", {"start": v(27.48, -0.85) * mm, "end": v(28.14, -0.43) * mm});
            skLineSegment(sketch, "E51.10.8", {"start": v(24.74, -2.11) * mm, "end": v(25.2, -1.96) * mm});
            skLineSegment(sketch, "E51.10.9", {"start": v(27.42, -2.02) * mm, "end": v(28.03, -2.5) * mm});
            skLineSegment(sketch, "E51.10.10", {"start": v(26.86, -1.21) * mm, "end": v(27.48, -0.85) * mm});
            skLineSegment(sketch, "E51.10.11", {"start": v(25.27, -0.69) * mm, "end": v(25.76, -0.94) * mm});
            skLineSegment(sketch, "E51.10.12", {"start": v(26.84, -1.6) * mm, "end": v(27.42, -2.02) * mm});
            skLineSegment(sketch, "E51.10.13", {"start": v(23.65, -2.37) * mm, "end": v(23.96, -2.31) * mm});
            skLineSegment(sketch, "E51.10.14", {"start": v(23.96, -2.31) * mm, "end": v(24.32, -2.23) * mm});
            skLineSegment(sketch, "E51.10.15", {"start": v(24.32, -2.23) * mm, "end": v(24.74, -2.11) * mm});
            skLineSegment(sketch, "E51.10.16", {"start": v(24.42, -0.33) * mm, "end": v(24.83, -0.48) * mm});
            skLineSegment(sketch, "E51.10.17", {"start": v(24.07, -0.2) * mm, "end": v(24.42, -0.33) * mm});
            skLineSegment(sketch, "E51.10.18", {"start": v(24.83, -0.48) * mm, "end": v(25.27, -0.69) * mm});
            skLineSegment(sketch, "E51.10.19", {"start": v(23.39, -2.4) * mm, "end": v(23.65, -2.37) * mm});
            skLineSegment(sketch, "E51.10.20", {"start": v(23.19, -2.41) * mm, "end": v(23.39, -2.4) * mm});
            skLineSegment(sketch, "E51.10.21", {"start": v(23.76, -0.12) * mm, "end": v(24.07, -0.2) * mm});
            skLineSegment(sketch, "E51.10.22", {"start": v(23.51, -0.06) * mm, "end": v(23.76, -0.12) * mm});
            skLineSegment(sketch, "E51.10.23", {"start": v(23.17, 0) * mm, "end": v(23.31, -0.03) * mm});
            skLineSegment(sketch, "E51.10.24", {"start": v(22.93, -2.4) * mm, "end": v(22.96, -2.41) * mm});
            skLineSegment(sketch, "E51.10.25", {"start": v(22.96, -2.41) * mm, "end": v(23.04, -2.41) * mm});
            skLineSegment(sketch, "E51.10.26", {"start": v(23.31, -0.03) * mm, "end": v(23.51, -0.06) * mm});
            skLineSegment(sketch, "E51.10.27", {"start": v(23.04, -2.41) * mm, "end": v(23.19, -2.41) * mm});
            skLineSegment(sketch, "E51.10.28", {"start": v(23.08, 0) * mm, "end": v(23.17, 0) * mm});
            skLineSegment(sketch, "E51.10.29", {"start": v(23.05, 0) * mm, "end": v(23.08, 0) * mm});
            skLineSegment(sketch, "E51.11.0", {"start": v(20.9, 6.8) * mm, "end": v(21.93, 7.12) * mm});
            skLineSegment(sketch, "E51.11.1", {"start": v(25.45, 6.68) * mm, "end": v(25.92, 7.15) * mm});
            skLineSegment(sketch, "E51.11.2", {"start": v(21.5, 4.57) * mm, "end": v(22.55, 4.8) * mm});
            skLineSegment(sketch, "E51.11.3", {"start": v(25, 6.27) * mm, "end": v(25.45, 6.68) * mm});
            skLineSegment(sketch, "E51.11.4", {"start": v(24.79, 7.07) * mm, "end": v(25.38, 6.94) * mm});
            skLineSegment(sketch, "E51.11.5", {"start": v(25.38, 6.94) * mm, "end": v(26.02, 6.77) * mm});
            skLineSegment(sketch, "E51.11.6", {"start": v(24.58, 5.93) * mm, "end": v(25, 6.27) * mm});
            skLineSegment(sketch, "E51.11.7", {"start": v(26.4, 7.68) * mm, "end": v(26.9, 8.28) * mm});
            skLineSegment(sketch, "E51.11.8", {"start": v(24.18, 5.63) * mm, "end": v(24.58, 5.93) * mm});
            skLineSegment(sketch, "E51.11.9", {"start": v(26.7, 6.55) * mm, "end": v(27.43, 6.28) * mm});
            skLineSegment(sketch, "E51.11.10", {"start": v(25.92, 7.15) * mm, "end": v(26.4, 7.68) * mm});
            skLineSegment(sketch, "E51.11.11", {"start": v(24.25, 7.16) * mm, "end": v(24.79, 7.07) * mm});
            skLineSegment(sketch, "E51.11.12", {"start": v(26.02, 6.77) * mm, "end": v(26.7, 6.55) * mm});
            skLineSegment(sketch, "E51.11.13", {"start": v(23.22, 5.06) * mm, "end": v(23.5, 5.2) * mm});
            skLineSegment(sketch, "E51.11.14", {"start": v(23.5, 5.2) * mm, "end": v(23.82, 5.4) * mm});
            skLineSegment(sketch, "E51.11.15", {"start": v(23.82, 5.4) * mm, "end": v(24.18, 5.63) * mm});
            skLineSegment(sketch, "E51.11.16", {"start": v(23.33, 7.24) * mm, "end": v(23.76, 7.21) * mm});
            skLineSegment(sketch, "E51.11.17", {"start": v(22.95, 7.24) * mm, "end": v(23.33, 7.24) * mm});
            skLineSegment(sketch, "E51.11.18", {"start": v(23.76, 7.21) * mm, "end": v(24.25, 7.16) * mm});
            skLineSegment(sketch, "E51.11.19", {"start": v(22.98, 4.95) * mm, "end": v(23.22, 5.06) * mm});
            skLineSegment(sketch, "E51.11.20", {"start": v(22.8, 4.87) * mm, "end": v(22.98, 4.95) * mm});
            skLineSegment(sketch, "E51.11.21", {"start": v(22.64, 7.23) * mm, "end": v(22.95, 7.24) * mm});
            skLineSegment(sketch, "E51.11.22", {"start": v(22.38, 7.2) * mm, "end": v(22.64, 7.23) * mm});
            skLineSegment(sketch, "E51.11.23", {"start": v(22.04, 7.15) * mm, "end": v(22.18, 7.18) * mm});
            skLineSegment(sketch, "E51.11.24", {"start": v(22.55, 4.8) * mm, "end": v(22.58, 4.8) * mm});
            skLineSegment(sketch, "E51.11.25", {"start": v(22.58, 4.8) * mm, "end": v(22.66, 4.82) * mm});
            skLineSegment(sketch, "E51.11.26", {"start": v(22.18, 7.18) * mm, "end": v(22.38, 7.2) * mm});
            skLineSegment(sketch, "E51.11.27", {"start": v(22.66, 4.82) * mm, "end": v(22.8, 4.87) * mm});
            skLineSegment(sketch, "E51.11.28", {"start": v(21.95, 7.13) * mm, "end": v(22.04, 7.15) * mm});
            skLineSegment(sketch, "E51.11.29", {"start": v(21.93, 7.12) * mm, "end": v(21.95, 7.13) * mm});
            skLineSegment(sketch, "E51.12.0", {"start": v(17.78, 12.92) * mm, "end": v(18.65, 13.55) * mm});
            skLineSegment(sketch, "E51.12.1", {"start": v(22.14, 14.21) * mm, "end": v(22.44, 14.8) * mm});
            skLineSegment(sketch, "E51.12.2", {"start": v(19.03, 10.99) * mm, "end": v(19.97, 11.53) * mm});
            skLineSegment(sketch, "E51.12.3", {"start": v(21.84, 13.7) * mm, "end": v(22.14, 14.21) * mm});
            skLineSegment(sketch, "E51.12.4", {"start": v(21.39, 14.38) * mm, "end": v(22, 14.44) * mm});
            skLineSegment(sketch, "E51.12.5", {"start": v(22, 14.44) * mm, "end": v(22.65, 14.48) * mm});
            skLineSegment(sketch, "E51.12.6", {"start": v(21.54, 13.23) * mm, "end": v(21.84, 13.7) * mm});
            skLineSegment(sketch, "E51.12.7", {"start": v(22.74, 15.46) * mm, "end": v(23.02, 16.19) * mm});
            skLineSegment(sketch, "E51.12.8", {"start": v(21.26, 12.83) * mm, "end": v(21.54, 13.23) * mm});
            skLineSegment(sketch, "E51.12.9", {"start": v(23.37, 14.48) * mm, "end": v(24.15, 14.45) * mm});
            skLineSegment(sketch, "E51.12.10", {"start": v(22.44, 14.8) * mm, "end": v(22.74, 15.46) * mm});
            skLineSegment(sketch, "E51.12.11", {"start": v(20.85, 14.3) * mm, "end": v(21.39, 14.38) * mm});
            skLineSegment(sketch, "E51.12.12", {"start": v(22.65, 14.48) * mm, "end": v(23.37, 14.48) * mm});
            skLineSegment(sketch, "E51.12.13", {"start": v(20.52, 11.98) * mm, "end": v(20.74, 12.21) * mm});
            skLineSegment(sketch, "E51.12.14", {"start": v(20.74, 12.21) * mm, "end": v(20.99, 12.5) * mm});
            skLineSegment(sketch, "E51.12.15", {"start": v(20.99, 12.5) * mm, "end": v(21.26, 12.83) * mm});
            skLineSegment(sketch, "E51.12.16", {"start": v(19.95, 14.1) * mm, "end": v(20.37, 14.2) * mm});
            skLineSegment(sketch, "E51.12.17", {"start": v(19.6, 13.98) * mm, "end": v(19.95, 14.1) * mm});
            skLineSegment(sketch, "E51.12.18", {"start": v(20.37, 14.2) * mm, "end": v(20.85, 14.3) * mm});
            skLineSegment(sketch, "E51.12.19", {"start": v(20.33, 11.8) * mm, "end": v(20.52, 11.98) * mm});
            skLineSegment(sketch, "E51.12.20", {"start": v(20.18, 11.68) * mm, "end": v(20.33, 11.8) * mm});
            skLineSegment(sketch, "E51.12.21", {"start": v(19.3, 13.87) * mm, "end": v(19.6, 13.98) * mm});
            skLineSegment(sketch, "E51.12.22", {"start": v(19.06, 13.77) * mm, "end": v(19.3, 13.87) * mm});
            skLineSegment(sketch, "E51.12.23", {"start": v(18.75, 13.61) * mm, "end": v(18.87, 13.68) * mm});
            skLineSegment(sketch, "E51.12.24", {"start": v(19.97, 11.53) * mm, "end": v(19.99, 11.54) * mm});
            skLineSegment(sketch, "E51.12.25", {"start": v(19.99, 11.54) * mm, "end": v(20.06, 11.6) * mm});
            skLineSegment(sketch, "E51.12.26", {"start": v(18.87, 13.68) * mm, "end": v(19.06, 13.77) * mm});
            skLineSegment(sketch, "E51.12.27", {"start": v(20.06, 11.6) * mm, "end": v(20.18, 11.68) * mm});
            skLineSegment(sketch, "E51.12.28", {"start": v(18.67, 13.57) * mm, "end": v(18.75, 13.61) * mm});
            skLineSegment(sketch, "E51.12.29", {"start": v(18.65, 13.55) * mm, "end": v(18.67, 13.57) * mm});
            skLineSegment(sketch, "E51.13.0", {"start": v(12.92, 17.78) * mm, "end": v(13.55, 18.65) * mm});
            skLineSegment(sketch, "E51.13.1", {"start": v(16.66, 20.36) * mm, "end": v(16.77, 21.02) * mm});
            skLineSegment(sketch, "E51.13.2", {"start": v(14.7, 16.33) * mm, "end": v(15.43, 17.13) * mm});
            skLineSegment(sketch, "E51.13.3", {"start": v(16.54, 19.77) * mm, "end": v(16.66, 20.36) * mm});
            skLineSegment(sketch, "E51.13.4", {"start": v(15.9, 20.29) * mm, "end": v(16.45, 20.53) * mm});
            skLineSegment(sketch, "E51.13.5", {"start": v(16.45, 20.53) * mm, "end": v(17.07, 20.77) * mm});
            skLineSegment(sketch, "E51.13.6", {"start": v(16.4, 19.24) * mm, "end": v(16.54, 19.77) * mm});
            skLineSegment(sketch, "E51.13.7", {"start": v(16.85, 21.73) * mm, "end": v(16.9, 22.5) * mm});
            skLineSegment(sketch, "E51.13.8", {"start": v(16.25, 18.77) * mm, "end": v(16.4, 19.24) * mm});
            skLineSegment(sketch, "E51.13.9", {"start": v(17.75, 21) * mm, "end": v(18.5, 21.2) * mm});
            skLineSegment(sketch, "E51.13.10", {"start": v(16.77, 21.02) * mm, "end": v(16.85, 21.73) * mm});
            skLineSegment(sketch, "E51.13.11", {"start": v(15.4, 20.04) * mm, "end": v(15.9, 20.29) * mm});
            skLineSegment(sketch, "E51.13.12", {"start": v(17.07, 20.77) * mm, "end": v(17.75, 21) * mm});
            skLineSegment(sketch, "E51.13.13", {"start": v(15.81, 17.74) * mm, "end": v(15.95, 18.02) * mm});
            skLineSegment(sketch, "E51.13.14", {"start": v(15.95, 18.02) * mm, "end": v(16.1, 18.37) * mm});
            skLineSegment(sketch, "E51.13.15", {"start": v(16.1, 18.37) * mm, "end": v(16.25, 18.77) * mm});
            skLineSegment(sketch, "E51.13.16", {"start": v(14.62, 19.57) * mm, "end": v(14.98, 19.8) * mm});
            skLineSegment(sketch, "E51.13.17", {"start": v(14.31, 19.35) * mm, "end": v(14.62, 19.57) * mm});
            skLineSegment(sketch, "E51.13.18", {"start": v(14.98, 19.8) * mm, "end": v(15.4, 20.04) * mm});
            skLineSegment(sketch, "E51.13.19", {"start": v(15.69, 17.51) * mm, "end": v(15.81, 17.74) * mm});
            skLineSegment(sketch, "E51.13.20", {"start": v(15.58, 17.34) * mm, "end": v(15.69, 17.51) * mm});
            skLineSegment(sketch, "E51.13.21", {"start": v(14.06, 19.15) * mm, "end": v(14.31, 19.35) * mm});
            skLineSegment(sketch, "E51.13.22", {"start": v(13.87, 18.98) * mm, "end": v(14.06, 19.15) * mm});
            skLineSegment(sketch, "E51.13.23", {"start": v(13.62, 18.74) * mm, "end": v(13.72, 18.84) * mm});
            skLineSegment(sketch, "E51.13.24", {"start": v(15.43, 17.13) * mm, "end": v(15.44, 17.15) * mm});
            skLineSegment(sketch, "E51.13.25", {"start": v(15.44, 17.15) * mm, "end": v(15.5, 17.22) * mm});
            skLineSegment(sketch, "E51.13.26", {"start": v(13.72, 18.84) * mm, "end": v(13.87, 18.98) * mm});
            skLineSegment(sketch, "E51.13.27", {"start": v(15.5, 17.22) * mm, "end": v(15.58, 17.34) * mm});
            skLineSegment(sketch, "E51.13.28", {"start": v(13.57, 18.67) * mm, "end": v(13.62, 18.74) * mm});
            skLineSegment(sketch, "E51.13.29", {"start": v(13.55, 18.65) * mm, "end": v(13.57, 18.67) * mm});
            skLineSegment(sketch, "E51.14.0", {"start": v(6.8, 20.9) * mm, "end": v(7.12, 21.93) * mm});
            skLineSegment(sketch, "E51.14.1", {"start": v(9.56, 24.51) * mm, "end": v(9.45, 25.17) * mm});
            skLineSegment(sketch, "E51.14.2", {"start": v(8.94, 20.08) * mm, "end": v(9.38, 21.06) * mm});
            skLineSegment(sketch, "E51.14.3", {"start": v(9.62, 23.91) * mm, "end": v(9.56, 24.51) * mm});
            skLineSegment(sketch, "E51.14.4", {"start": v(8.85, 24.2) * mm, "end": v(9.3, 24.61) * mm});
            skLineSegment(sketch, "E51.14.5", {"start": v(9.3, 24.61) * mm, "end": v(9.82, 25.03) * mm});
            skLineSegment(sketch, "E51.14.6", {"start": v(9.65, 23.37) * mm, "end": v(9.62, 23.91) * mm});
            skLineSegment(sketch, "E51.14.7", {"start": v(9.3, 25.87) * mm, "end": v(9.1, 26.63) * mm});
            skLineSegment(sketch, "E51.14.8", {"start": v(9.66, 22.88) * mm, "end": v(9.65, 23.37) * mm});
            skLineSegment(sketch, "E51.14.9", {"start": v(10.4, 25.45) * mm, "end": v(11.05, 25.88) * mm});
            skLineSegment(sketch, "E51.14.10", {"start": v(9.45, 25.17) * mm, "end": v(9.3, 25.87) * mm});
            skLineSegment(sketch, "E51.14.11", {"start": v(8.46, 23.82) * mm, "end": v(8.85, 24.2) * mm});
            skLineSegment(sketch, "E51.14.12", {"start": v(9.82, 25.03) * mm, "end": v(10.4, 25.45) * mm});
            skLineSegment(sketch, "E51.14.13", {"start": v(9.56, 21.76) * mm, "end": v(9.6, 22.07) * mm});
            skLineSegment(sketch, "E51.14.14", {"start": v(9.6, 22.07) * mm, "end": v(9.64, 22.44) * mm});
            skLineSegment(sketch, "E51.14.15", {"start": v(9.64, 22.44) * mm, "end": v(9.66, 22.88) * mm});
            skLineSegment(sketch, "E51.14.16", {"start": v(7.86, 23.13) * mm, "end": v(8.13, 23.46) * mm});
            skLineSegment(sketch, "E51.14.17", {"start": v(7.63, 22.83) * mm, "end": v(7.86, 23.13) * mm});
            skLineSegment(sketch, "E51.14.18", {"start": v(8.13, 23.46) * mm, "end": v(8.46, 23.82) * mm});
            skLineSegment(sketch, "E51.14.19", {"start": v(9.5, 21.5) * mm, "end": v(9.56, 21.76) * mm});
            skLineSegment(sketch, "E51.14.20", {"start": v(9.46, 21.3) * mm, "end": v(9.5, 21.5) * mm});
            skLineSegment(sketch, "E51.14.21", {"start": v(7.46, 22.56) * mm, "end": v(7.63, 22.83) * mm});
            skLineSegment(sketch, "E51.14.22", {"start": v(7.32, 22.34) * mm, "end": v(7.46, 22.56) * mm});
            skLineSegment(sketch, "E51.14.23", {"start": v(7.17, 22.03) * mm, "end": v(7.23, 22.16) * mm});
            skLineSegment(sketch, "E51.14.24", {"start": v(9.38, 21.06) * mm, "end": v(9.39, 21.09) * mm});
            skLineSegment(sketch, "E51.14.25", {"start": v(9.39, 21.09) * mm, "end": v(9.42, 21.17) * mm});
            skLineSegment(sketch, "E51.14.26", {"start": v(7.23, 22.16) * mm, "end": v(7.32, 22.34) * mm});
            skLineSegment(sketch, "E51.14.27", {"start": v(9.42, 21.17) * mm, "end": v(9.46, 21.3) * mm});
            skLineSegment(sketch, "E51.14.28", {"start": v(7.13, 21.95) * mm, "end": v(7.17, 22.03) * mm});
            skLineSegment(sketch, "E51.14.29", {"start": v(7.12, 21.93) * mm, "end": v(7.13, 21.95) * mm});
            skLineSegment(sketch, "E51.15.0", {"start": v(0, 21.98) * mm, "end": v(0, 23.05) * mm});
            skLineSegment(sketch, "E51.15.1", {"start": v(1.51, 26.27) * mm, "end": v(1.21, 26.86) * mm});
            skLineSegment(sketch, "E51.15.2", {"start": v(2.3, 21.86) * mm, "end": v(2.4, 22.93) * mm});
            skLineSegment(sketch, "E51.15.3", {"start": v(1.76, 25.71) * mm, "end": v(1.51, 26.27) * mm});
            skLineSegment(sketch, "E51.15.4", {"start": v(0.94, 25.76) * mm, "end": v(1.24, 26.28) * mm});
            skLineSegment(sketch, "E51.15.5", {"start": v(1.24, 26.28) * mm, "end": v(1.6, 26.84) * mm});
            skLineSegment(sketch, "E51.15.6", {"start": v(1.96, 25.2) * mm, "end": v(1.76, 25.71) * mm});
            skLineSegment(sketch, "E51.15.7", {"start": v(0.85, 27.48) * mm, "end": v(0.43, 28.14) * mm});
            skLineSegment(sketch, "E51.15.8", {"start": v(2.11, 24.74) * mm, "end": v(1.96, 25.2) * mm});
            skLineSegment(sketch, "E51.15.9", {"start": v(2.02, 27.42) * mm, "end": v(2.5, 28.03) * mm});
            skLineSegment(sketch, "E51.15.10", {"start": v(1.21, 26.86) * mm, "end": v(0.85, 27.48) * mm});
            skLineSegment(sketch, "E51.15.11", {"start": v(0.69, 25.27) * mm, "end": v(0.94, 25.76) * mm});
            skLineSegment(sketch, "E51.15.12", {"start": v(1.6, 26.84) * mm, "end": v(2.02, 27.42) * mm});
            skLineSegment(sketch, "E51.15.13", {"start": v(2.37, 23.65) * mm, "end": v(2.31, 23.96) * mm});
            skLineSegment(sketch, "E51.15.14", {"start": v(2.31, 23.96) * mm, "end": v(2.23, 24.32) * mm});
            skLineSegment(sketch, "E51.15.15", {"start": v(2.23, 24.32) * mm, "end": v(2.11, 24.74) * mm});
            skLineSegment(sketch, "E51.15.16", {"start": v(0.33, 24.42) * mm, "end": v(0.48, 24.83) * mm});
            skLineSegment(sketch, "E51.15.17", {"start": v(0.2, 24.07) * mm, "end": v(0.33, 24.42) * mm});
            skLineSegment(sketch, "E51.15.18", {"start": v(0.48, 24.83) * mm, "end": v(0.69, 25.27) * mm});
            skLineSegment(sketch, "E51.15.19", {"start": v(2.4, 23.39) * mm, "end": v(2.37, 23.65) * mm});
            skLineSegment(sketch, "E51.15.20", {"start": v(2.41, 23.19) * mm, "end": v(2.4, 23.39) * mm});
            skLineSegment(sketch, "E51.15.21", {"start": v(0.12, 23.76) * mm, "end": v(0.2, 24.07) * mm});
            skLineSegment(sketch, "E51.15.22", {"start": v(0.06, 23.51) * mm, "end": v(0.12, 23.76) * mm});
            skLineSegment(sketch, "E51.15.23", {"start": v(0, 23.17) * mm, "end": v(0.03, 23.31) * mm});
            skLineSegment(sketch, "E51.15.24", {"start": v(2.4, 22.93) * mm, "end": v(2.41, 22.96) * mm});
            skLineSegment(sketch, "E51.15.25", {"start": v(2.41, 22.96) * mm, "end": v(2.41, 23.04) * mm});
            skLineSegment(sketch, "E51.15.26", {"start": v(0.03, 23.31) * mm, "end": v(0.06, 23.51) * mm});
            skLineSegment(sketch, "E51.15.27", {"start": v(2.41, 23.04) * mm, "end": v(2.41, 23.19) * mm});
            skLineSegment(sketch, "E51.15.28", {"start": v(0, 23.08) * mm, "end": v(0, 23.17) * mm});
            skLineSegment(sketch, "E51.15.29", {"start": v(0, 23.05) * mm, "end": v(0, 23.08) * mm});
            skLineSegment(sketch, "E51.16.0", {"start": v(-6.8, 20.9) * mm, "end": v(-7.12, 21.93) * mm});
            skLineSegment(sketch, "E51.16.1", {"start": v(-6.68, 25.45) * mm, "end": v(-7.15, 25.92) * mm});
            skLineSegment(sketch, "E51.16.2", {"start": v(-4.57, 21.5) * mm, "end": v(-4.8, 22.55) * mm});
            skLineSegment(sketch, "E51.16.3", {"start": v(-6.27, 25) * mm, "end": v(-6.68, 25.45) * mm});
            skLineSegment(sketch, "E51.16.4", {"start": v(-7.07, 24.79) * mm, "end": v(-6.94, 25.38) * mm});
            skLineSegment(sketch, "E51.16.5", {"start": v(-6.94, 25.38) * mm, "end": v(-6.77, 26.02) * mm});
            skLineSegment(sketch, "E51.16.6", {"start": v(-5.93, 24.58) * mm, "end": v(-6.27, 25) * mm});
            skLineSegment(sketch, "E51.16.7", {"start": v(-7.68, 26.4) * mm, "end": v(-8.28, 26.9) * mm});
            skLineSegment(sketch, "E51.16.8", {"start": v(-5.63, 24.18) * mm, "end": v(-5.93, 24.58) * mm});
            skLineSegment(sketch, "E51.16.9", {"start": v(-6.55, 26.7) * mm, "end": v(-6.28, 27.43) * mm});
            skLineSegment(sketch, "E51.16.10", {"start": v(-7.15, 25.92) * mm, "end": v(-7.68, 26.4) * mm});
            skLineSegment(sketch, "E51.16.11", {"start": v(-7.16, 24.25) * mm, "end": v(-7.07, 24.79) * mm});
            skLineSegment(sketch, "E51.16.12", {"start": v(-6.77, 26.02) * mm, "end": v(-6.55, 26.7) * mm});
            skLineSegment(sketch, "E51.16.13", {"start": v(-5.06, 23.22) * mm, "end": v(-5.2, 23.5) * mm});
            skLineSegment(sketch, "E51.16.14", {"start": v(-5.2, 23.5) * mm, "end": v(-5.4, 23.82) * mm});
            skLineSegment(sketch, "E51.16.15", {"start": v(-5.4, 23.82) * mm, "end": v(-5.63, 24.18) * mm});
            skLineSegment(sketch, "E51.16.16", {"start": v(-7.24, 23.33) * mm, "end": v(-7.21, 23.76) * mm});
            skLineSegment(sketch, "E51.16.17", {"start": v(-7.24, 22.95) * mm, "end": v(-7.24, 23.33) * mm});
            skLineSegment(sketch, "E51.16.18", {"start": v(-7.21, 23.76) * mm, "end": v(-7.16, 24.25) * mm});
            skLineSegment(sketch, "E51.16.19", {"start": v(-4.95, 22.98) * mm, "end": v(-5.06, 23.22) * mm});
            skLineSegment(sketch, "E51.16.20", {"start": v(-4.87, 22.8) * mm, "end": v(-4.95, 22.98) * mm});
            skLineSegment(sketch, "E51.16.21", {"start": v(-7.23, 22.64) * mm, "end": v(-7.24, 22.95) * mm});
            skLineSegment(sketch, "E51.16.22", {"start": v(-7.2, 22.38) * mm, "end": v(-7.23, 22.64) * mm});
            skLineSegment(sketch, "E51.16.23", {"start": v(-7.15, 22.04) * mm, "end": v(-7.18, 22.18) * mm});
            skLineSegment(sketch, "E51.16.24", {"start": v(-4.8, 22.55) * mm, "end": v(-4.8, 22.58) * mm});
            skLineSegment(sketch, "E51.16.25", {"start": v(-4.8, 22.58) * mm, "end": v(-4.82, 22.66) * mm});
            skLineSegment(sketch, "E51.16.26", {"start": v(-7.18, 22.18) * mm, "end": v(-7.2, 22.38) * mm});
            skLineSegment(sketch, "E51.16.27", {"start": v(-4.82, 22.66) * mm, "end": v(-4.87, 22.8) * mm});
            skLineSegment(sketch, "E51.16.28", {"start": v(-7.13, 21.95) * mm, "end": v(-7.15, 22.04) * mm});
            skLineSegment(sketch, "E51.16.29", {"start": v(-7.12, 21.93) * mm, "end": v(-7.13, 21.95) * mm});
            skLineSegment(sketch, "E51.17.0", {"start": v(-12.92, 17.78) * mm, "end": v(-13.55, 18.65) * mm});
            skLineSegment(sketch, "E51.17.1", {"start": v(-14.21, 22.14) * mm, "end": v(-14.8, 22.44) * mm});
            skLineSegment(sketch, "E51.17.2", {"start": v(-10.99, 19.03) * mm, "end": v(-11.53, 19.97) * mm});
            skLineSegment(sketch, "E51.17.3", {"start": v(-13.7, 21.84) * mm, "end": v(-14.21, 22.14) * mm});
            skLineSegment(sketch, "E51.17.4", {"start": v(-14.38, 21.39) * mm, "end": v(-14.44, 22) * mm});
            skLineSegment(sketch, "E51.17.5", {"start": v(-14.44, 22) * mm, "end": v(-14.48, 22.65) * mm});
            skLineSegment(sketch, "E51.17.6", {"start": v(-13.23, 21.54) * mm, "end": v(-13.7, 21.84) * mm});
            skLineSegment(sketch, "E51.17.7", {"start": v(-15.46, 22.74) * mm, "end": v(-16.19, 23.02) * mm});
            skLineSegment(sketch, "E51.17.8", {"start": v(-12.83, 21.26) * mm, "end": v(-13.23, 21.54) * mm});
            skLineSegment(sketch, "E51.17.9", {"start": v(-14.48, 23.37) * mm, "end": v(-14.45, 24.15) * mm});
            skLineSegment(sketch, "E51.17.10", {"start": v(-14.8, 22.44) * mm, "end": v(-15.46, 22.74) * mm});
            skLineSegment(sketch, "E51.17.11", {"start": v(-14.3, 20.85) * mm, "end": v(-14.38, 21.39) * mm});
            skLineSegment(sketch, "E51.17.12", {"start": v(-14.48, 22.65) * mm, "end": v(-14.48, 23.37) * mm});
            skLineSegment(sketch, "E51.17.13", {"start": v(-11.98, 20.52) * mm, "end": v(-12.21, 20.74) * mm});
            skLineSegment(sketch, "E51.17.14", {"start": v(-12.21, 20.74) * mm, "end": v(-12.5, 20.99) * mm});
            skLineSegment(sketch, "E51.17.15", {"start": v(-12.5, 20.99) * mm, "end": v(-12.83, 21.26) * mm});
            skLineSegment(sketch, "E51.17.16", {"start": v(-14.1, 19.95) * mm, "end": v(-14.2, 20.37) * mm});
            skLineSegment(sketch, "E51.17.17", {"start": v(-13.98, 19.6) * mm, "end": v(-14.1, 19.95) * mm});
            skLineSegment(sketch, "E51.17.18", {"start": v(-14.2, 20.37) * mm, "end": v(-14.3, 20.85) * mm});
            skLineSegment(sketch, "E51.17.19", {"start": v(-11.8, 20.33) * mm, "end": v(-11.98, 20.52) * mm});
            skLineSegment(sketch, "E51.17.20", {"start": v(-11.68, 20.18) * mm, "end": v(-11.8, 20.33) * mm});
            skLineSegment(sketch, "E51.17.21", {"start": v(-13.87, 19.3) * mm, "end": v(-13.98, 19.6) * mm});
            skLineSegment(sketch, "E51.17.22", {"start": v(-13.77, 19.06) * mm, "end": v(-13.87, 19.3) * mm});
            skLineSegment(sketch, "E51.17.23", {"start": v(-13.61, 18.75) * mm, "end": v(-13.68, 18.87) * mm});
            skLineSegment(sketch, "E51.17.24", {"start": v(-11.53, 19.97) * mm, "end": v(-11.54, 19.99) * mm});
            skLineSegment(sketch, "E51.17.25", {"start": v(-11.54, 19.99) * mm, "end": v(-11.6, 20.06) * mm});
            skLineSegment(sketch, "E51.17.26", {"start": v(-13.68, 18.87) * mm, "end": v(-13.77, 19.06) * mm});
            skLineSegment(sketch, "E51.17.27", {"start": v(-11.6, 20.06) * mm, "end": v(-11.68, 20.18) * mm});
            skLineSegment(sketch, "E51.17.28", {"start": v(-13.57, 18.67) * mm, "end": v(-13.61, 18.75) * mm});
            skLineSegment(sketch, "E51.17.29", {"start": v(-13.55, 18.65) * mm, "end": v(-13.57, 18.67) * mm});
            skLineSegment(sketch, "E51.18.0", {"start": v(-17.78, 12.92) * mm, "end": v(-18.65, 13.55) * mm});
            skLineSegment(sketch, "E51.18.1", {"start": v(-20.36, 16.66) * mm, "end": v(-21.02, 16.77) * mm});
            skLineSegment(sketch, "E51.18.2", {"start": v(-16.33, 14.7) * mm, "end": v(-17.13, 15.43) * mm});
            skLineSegment(sketch, "E51.18.3", {"start": v(-19.77, 16.54) * mm, "end": v(-20.36, 16.66) * mm});
            skLineSegment(sketch, "E51.18.4", {"start": v(-20.29, 15.9) * mm, "end": v(-20.53, 16.45) * mm});
            skLineSegment(sketch, "E51.18.5", {"start": v(-20.53, 16.45) * mm, "end": v(-20.77, 17.07) * mm});
            skLineSegment(sketch, "E51.18.6", {"start": v(-19.24, 16.4) * mm, "end": v(-19.77, 16.54) * mm});
            skLineSegment(sketch, "E51.18.7", {"start": v(-21.73, 16.85) * mm, "end": v(-22.5, 16.9) * mm});
            skLineSegment(sketch, "E51.18.8", {"start": v(-18.77, 16.25) * mm, "end": v(-19.24, 16.4) * mm});
            skLineSegment(sketch, "E51.18.9", {"start": v(-21, 17.75) * mm, "end": v(-21.2, 18.5) * mm});
            skLineSegment(sketch, "E51.18.10", {"start": v(-21.02, 16.77) * mm, "end": v(-21.73, 16.85) * mm});
            skLineSegment(sketch, "E51.18.11", {"start": v(-20.04, 15.4) * mm, "end": v(-20.29, 15.9) * mm});
            skLineSegment(sketch, "E51.18.12", {"start": v(-20.77, 17.07) * mm, "end": v(-21, 17.75) * mm});
            skLineSegment(sketch, "E51.18.13", {"start": v(-17.74, 15.81) * mm, "end": v(-18.02, 15.95) * mm});
            skLineSegment(sketch, "E51.18.14", {"start": v(-18.02, 15.95) * mm, "end": v(-18.37, 16.1) * mm});
            skLineSegment(sketch, "E51.18.15", {"start": v(-18.37, 16.1) * mm, "end": v(-18.77, 16.25) * mm});
            skLineSegment(sketch, "E51.18.16", {"start": v(-19.57, 14.62) * mm, "end": v(-19.8, 14.98) * mm});
            skLineSegment(sketch, "E51.18.17", {"start": v(-19.35, 14.31) * mm, "end": v(-19.57, 14.62) * mm});
            skLineSegment(sketch, "E51.18.18", {"start": v(-19.8, 14.98) * mm, "end": v(-20.04, 15.4) * mm});
            skLineSegment(sketch, "E51.18.19", {"start": v(-17.51, 15.69) * mm, "end": v(-17.74, 15.81) * mm});
            skLineSegment(sketch, "E51.18.20", {"start": v(-17.34, 15.58) * mm, "end": v(-17.51, 15.69) * mm});
            skLineSegment(sketch, "E51.18.21", {"start": v(-19.15, 14.06) * mm, "end": v(-19.35, 14.31) * mm});
            skLineSegment(sketch, "E51.18.22", {"start": v(-18.98, 13.87) * mm, "end": v(-19.15, 14.06) * mm});
            skLineSegment(sketch, "E51.18.23", {"start": v(-18.74, 13.62) * mm, "end": v(-18.84, 13.72) * mm});
            skLineSegment(sketch, "E51.18.24", {"start": v(-17.13, 15.43) * mm, "end": v(-17.15, 15.44) * mm});
            skLineSegment(sketch, "E51.18.25", {"start": v(-17.15, 15.44) * mm, "end": v(-17.22, 15.5) * mm});
            skLineSegment(sketch, "E51.18.26", {"start": v(-18.84, 13.72) * mm, "end": v(-18.98, 13.87) * mm});
            skLineSegment(sketch, "E51.18.27", {"start": v(-17.22, 15.5) * mm, "end": v(-17.34, 15.58) * mm});
            skLineSegment(sketch, "E51.18.28", {"start": v(-18.67, 13.57) * mm, "end": v(-18.74, 13.62) * mm});
            skLineSegment(sketch, "E51.18.29", {"start": v(-18.65, 13.55) * mm, "end": v(-18.67, 13.57) * mm});
            skLineSegment(sketch, "E51.19.0", {"start": v(-20.9, 6.8) * mm, "end": v(-21.93, 7.12) * mm});
            skLineSegment(sketch, "E51.19.1", {"start": v(-24.51, 9.56) * mm, "end": v(-25.17, 9.45) * mm});
            skLineSegment(sketch, "E51.19.2", {"start": v(-20.08, 8.94) * mm, "end": v(-21.06, 9.38) * mm});
            skLineSegment(sketch, "E51.19.3", {"start": v(-23.91, 9.62) * mm, "end": v(-24.51, 9.56) * mm});
            skLineSegment(sketch, "E51.19.4", {"start": v(-24.2, 8.85) * mm, "end": v(-24.61, 9.3) * mm});
            skLineSegment(sketch, "E51.19.5", {"start": v(-24.61, 9.3) * mm, "end": v(-25.03, 9.82) * mm});
            skLineSegment(sketch, "E51.19.6", {"start": v(-23.37, 9.65) * mm, "end": v(-23.91, 9.62) * mm});
            skLineSegment(sketch, "E51.19.7", {"start": v(-25.87, 9.3) * mm, "end": v(-26.63, 9.1) * mm});
            skLineSegment(sketch, "E51.19.8", {"start": v(-22.88, 9.66) * mm, "end": v(-23.37, 9.65) * mm});
            skLineSegment(sketch, "E51.19.9", {"start": v(-25.45, 10.4) * mm, "end": v(-25.88, 11.05) * mm});
            skLineSegment(sketch, "E51.19.10", {"start": v(-25.17, 9.45) * mm, "end": v(-25.87, 9.3) * mm});
            skLineSegment(sketch, "E51.19.11", {"start": v(-23.82, 8.46) * mm, "end": v(-24.2, 8.85) * mm});
            skLineSegment(sketch, "E51.19.12", {"start": v(-25.03, 9.82) * mm, "end": v(-25.45, 10.4) * mm});
            skLineSegment(sketch, "E51.19.13", {"start": v(-21.76, 9.56) * mm, "end": v(-22.07, 9.6) * mm});
            skLineSegment(sketch, "E51.19.14", {"start": v(-22.07, 9.6) * mm, "end": v(-22.44, 9.64) * mm});
            skLineSegment(sketch, "E51.19.15", {"start": v(-22.44, 9.64) * mm, "end": v(-22.88, 9.66) * mm});
            skLineSegment(sketch, "E51.19.16", {"start": v(-23.13, 7.86) * mm, "end": v(-23.46, 8.13) * mm});
            skLineSegment(sketch, "E51.19.17", {"start": v(-22.83, 7.63) * mm, "end": v(-23.13, 7.86) * mm});
            skLineSegment(sketch, "E51.19.18", {"start": v(-23.46, 8.13) * mm, "end": v(-23.82, 8.46) * mm});
            skLineSegment(sketch, "E51.19.19", {"start": v(-21.5, 9.5) * mm, "end": v(-21.76, 9.56) * mm});
            skLineSegment(sketch, "E51.19.20", {"start": v(-21.3, 9.46) * mm, "end": v(-21.5, 9.5) * mm});
            skLineSegment(sketch, "E51.19.21", {"start": v(-22.56, 7.46) * mm, "end": v(-22.83, 7.63) * mm});
            skLineSegment(sketch, "E51.19.22", {"start": v(-22.34, 7.32) * mm, "end": v(-22.56, 7.46) * mm});
            skLineSegment(sketch, "E51.19.23", {"start": v(-22.03, 7.17) * mm, "end": v(-22.16, 7.23) * mm});
            skLineSegment(sketch, "E51.19.24", {"start": v(-21.06, 9.38) * mm, "end": v(-21.09, 9.39) * mm});
            skLineSegment(sketch, "E51.19.25", {"start": v(-21.09, 9.39) * mm, "end": v(-21.17, 9.42) * mm});
            skLineSegment(sketch, "E51.19.26", {"start": v(-22.16, 7.23) * mm, "end": v(-22.34, 7.32) * mm});
            skLineSegment(sketch, "E51.19.27", {"start": v(-21.17, 9.42) * mm, "end": v(-21.3, 9.46) * mm});
            skLineSegment(sketch, "E51.19.28", {"start": v(-21.95, 7.13) * mm, "end": v(-22.03, 7.17) * mm});
            skLineSegment(sketch, "E51.19.29", {"start": v(-21.93, 7.12) * mm, "end": v(-21.95, 7.13) * mm});
            skSolve(sketch);
        }
        {
            var Q0;
            {var subQ0=sQuery(id+"F1.wireOp",EDGE,"E0");var subQ27=makeQuery(id+"F1.imprint","INTERSECT",VERTEX,{"derivedFrom":[subQ0,sQuery(id+"F1.wireOp",EDGE,"E51.10.0")]});Q0=makeQuery(id+"F1.imprint","IMPRINT",FACE,{"disambiguationData":[TD([[makeQuery(id+"F1.imprint","IMPRINT",EDGE,{"disambiguationData":[TD([[subQ27,-1.0]])],"derivedFrom":subQ0}),1.0]])]});}
            var Q1;
            {var subQ0=sQuery(id+"F1.wireOp",EDGE,"E51.1.0");Q1=makeQuery(id+"F1.imprint","IMPRINT",FACE,{"disambiguationData":[TD([[makeQuery(id+"F1.imprint","IMPRINT",EDGE,{"derivedFrom":subQ0}),-1.0]])]});}
            var Q2;
            {var subQ7=sQuery(id+"F1.wireOp",EDGE,"E51.2.0");Q2=makeQuery(id+"F1.imprint","IMPRINT",FACE,{"disambiguationData":[TD([[makeQuery(id+"F1.imprint","IMPRINT",EDGE,{"derivedFrom":subQ7}),-1.0]])]});}
            var Q3;
            {var subQ8=sQuery(id+"F1.wireOp",EDGE,"E51.3.0");Q3=makeQuery(id+"F1.imprint","IMPRINT",FACE,{"disambiguationData":[TD([[makeQuery(id+"F1.imprint","IMPRINT",EDGE,{"derivedFrom":subQ8}),-1.0]])]});}
            var Q4;
            {var subQ2=sQuery(id+"F1.wireOp",EDGE,"E51.4.0");Q4=makeQuery(id+"F1.imprint","IMPRINT",FACE,{"disambiguationData":[TD([[makeQuery(id+"F1.imprint","IMPRINT",EDGE,{"derivedFrom":subQ2}),-1.0]])]});}
            var Q5;
            {var subQ8=sQuery(id+"F1.wireOp",EDGE,"E51.5.0");Q5=makeQuery(id+"F1.imprint","IMPRINT",FACE,{"disambiguationData":[TD([[makeQuery(id+"F1.imprint","IMPRINT",EDGE,{"derivedFrom":subQ8}),-1.0]])]});}
            var Q6;
            {var subQ3=sQuery(id+"F1.wireOp",EDGE,"E51.6.0");Q6=makeQuery(id+"F1.imprint","IMPRINT",FACE,{"disambiguationData":[TD([[makeQuery(id+"F1.imprint","IMPRINT",EDGE,{"derivedFrom":subQ3}),-1.0]])]});}
            var Q7;
            {var subQ0=sQuery(id+"F1.wireOp",EDGE,"E51.7.0");Q7=makeQuery(id+"F1.imprint","IMPRINT",FACE,{"disambiguationData":[TD([[makeQuery(id+"F1.imprint","IMPRINT",EDGE,{"derivedFrom":subQ0}),-1.0]])]});}
            var Q8;
            {var subQ5=sQuery(id+"F1.wireOp",EDGE,"E51.8.0");Q8=makeQuery(id+"F1.imprint","IMPRINT",FACE,{"disambiguationData":[TD([[makeQuery(id+"F1.imprint","IMPRINT",EDGE,{"derivedFrom":subQ5}),-1.0]])]});}
            var Q9;
            {var subQ1=sQuery(id+"F1.wireOp",EDGE,"E51.9.0");Q9=makeQuery(id+"F1.imprint","IMPRINT",FACE,{"disambiguationData":[TD([[makeQuery(id+"F1.imprint","IMPRINT",EDGE,{"derivedFrom":subQ1}),-1.0]])]});}
            var Q10;
            {var subQ5=sQuery(id+"F1.wireOp",EDGE,"E51.10.0");Q10=makeQuery(id+"F1.imprint","IMPRINT",FACE,{"disambiguationData":[TD([[makeQuery(id+"F1.imprint","IMPRINT",EDGE,{"derivedFrom":subQ5}),-1.0]])]});}
            var Q11;
            {var subQ8=sQuery(id+"F1.wireOp",EDGE,"E51.11.0");Q11=makeQuery(id+"F1.imprint","IMPRINT",FACE,{"disambiguationData":[TD([[makeQuery(id+"F1.imprint","IMPRINT",EDGE,{"derivedFrom":subQ8}),-1.0]])]});}
            var Q12;
            {var subQ2=sQuery(id+"F1.wireOp",EDGE,"E51.12.0");Q12=makeQuery(id+"F1.imprint","IMPRINT",FACE,{"disambiguationData":[TD([[makeQuery(id+"F1.imprint","IMPRINT",EDGE,{"derivedFrom":subQ2}),-1.0]])]});}
            var Q13;
            {var subQ3=sQuery(id+"F1.wireOp",EDGE,"E51.13.0");Q13=makeQuery(id+"F1.imprint","IMPRINT",FACE,{"disambiguationData":[TD([[makeQuery(id+"F1.imprint","IMPRINT",EDGE,{"derivedFrom":subQ3}),-1.0]])]});}
            var Q14;
            {var subQ0=sQuery(id+"F1.wireOp",EDGE,"E51.14.0");Q14=makeQuery(id+"F1.imprint","IMPRINT",FACE,{"disambiguationData":[TD([[makeQuery(id+"F1.imprint","IMPRINT",EDGE,{"derivedFrom":subQ0}),-1.0]])]});}
            var Q15;
            {var subQ6=sQuery(id+"F1.wireOp",EDGE,"E51.15.0");Q15=makeQuery(id+"F1.imprint","IMPRINT",FACE,{"disambiguationData":[TD([[makeQuery(id+"F1.imprint","IMPRINT",EDGE,{"derivedFrom":subQ6}),-1.0]])]});}
            var Q16;
            {var subQ5=sQuery(id+"F1.wireOp",EDGE,"E51.16.0");Q16=makeQuery(id+"F1.imprint","IMPRINT",FACE,{"disambiguationData":[TD([[makeQuery(id+"F1.imprint","IMPRINT",EDGE,{"derivedFrom":subQ5}),-1.0]])]});}
            var Q17;
            {var subQ7=sQuery(id+"F1.wireOp",EDGE,"E51.17.0");Q17=makeQuery(id+"F1.imprint","IMPRINT",FACE,{"disambiguationData":[TD([[makeQuery(id+"F1.imprint","IMPRINT",EDGE,{"derivedFrom":subQ7}),-1.0]])]});}
            var Q18;
            {var subQ5=sQuery(id+"F1.wireOp",EDGE,"E51.18.0");Q18=makeQuery(id+"F1.imprint","IMPRINT",FACE,{"disambiguationData":[TD([[makeQuery(id+"F1.imprint","IMPRINT",EDGE,{"derivedFrom":subQ5}),-1.0]])]});}
            var Q19;
            {var subQ8=sQuery(id+"F1.wireOp",EDGE,"E51.19.0");Q19=makeQuery(id+"F1.imprint","IMPRINT",FACE,{"disambiguationData":[TD([[makeQuery(id+"F1.imprint","IMPRINT",EDGE,{"derivedFrom":subQ8}),-1.0]])]});}
            var Q20;
            {var subQ8=sQuery(id+"F1.wireOp",EDGE,"E21");Q20=makeQuery(id+"F1.imprint","IMPRINT",FACE,{"disambiguationData":[TD([[makeQuery(id+"F1.imprint","IMPRINT",EDGE,{"derivedFrom":subQ8}),-1.0]])]});}
            extrude(context, id + "F2", {"entities" : qUnion([Q0, Q1, Q2, Q3, Q4, Q5, Q6, Q7, Q8, Q9, Q10, Q11, Q12, Q13, Q14, Q15, Q16, Q17, Q18, Q19, Q20]), "depth" : (getVariable(context, 'GearThickness')) * mm});
        }
    });
